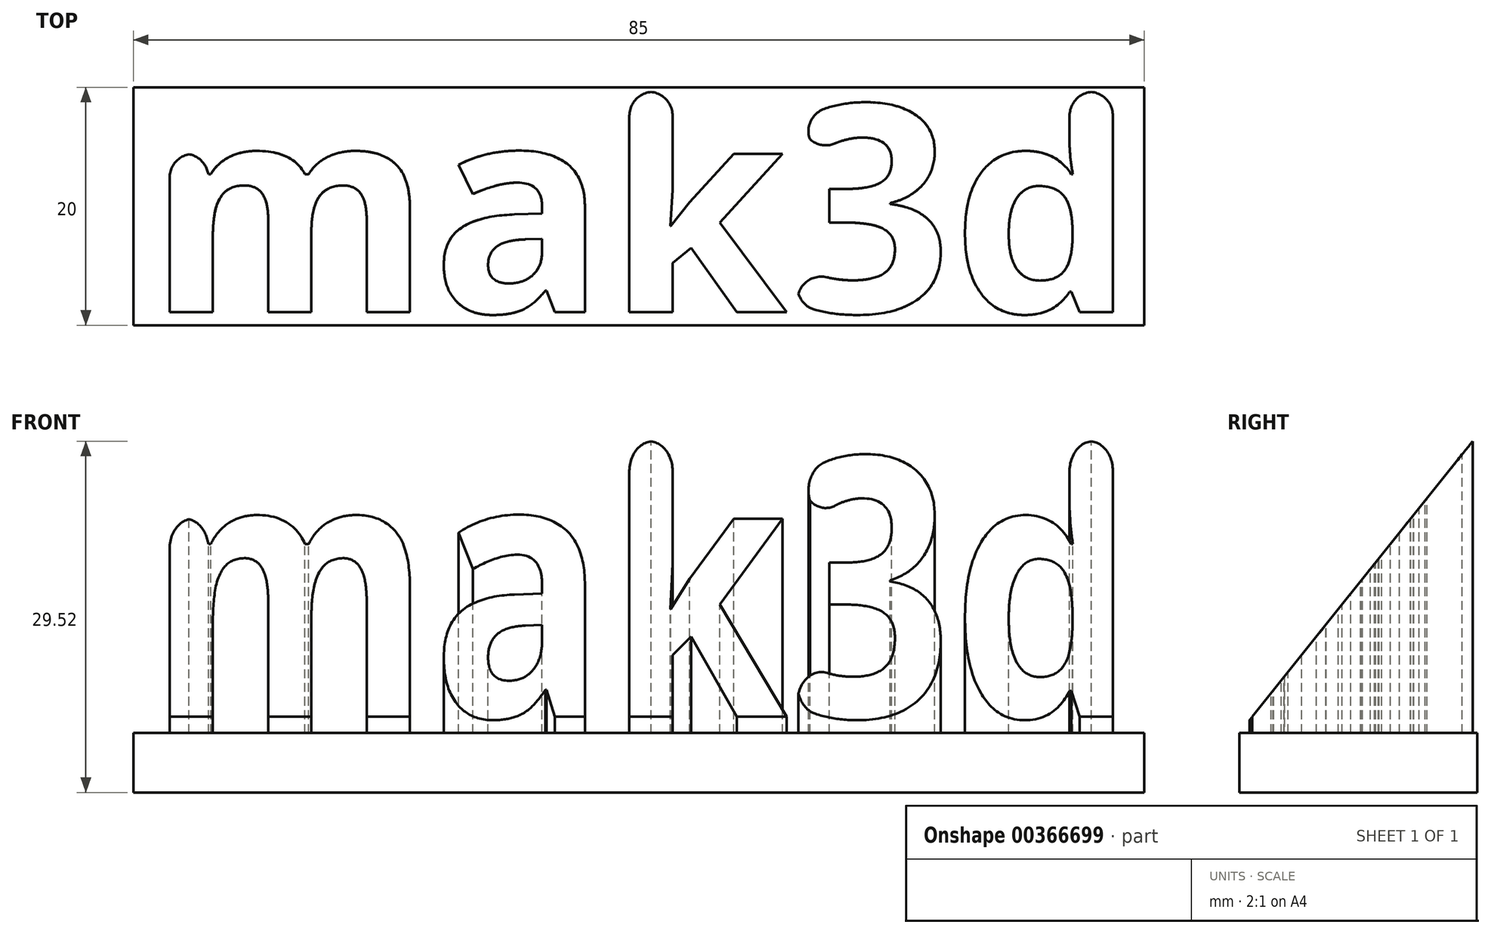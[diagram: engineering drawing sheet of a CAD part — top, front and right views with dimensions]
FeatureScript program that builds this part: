
annotation { "Feature Type Name" : "Feature", "Feature Type Description" : "" }
export const myFeature = defineFeature(function(context is Context, id is Id, definition is map)
    precondition{}
    {
        {
            var Q0;
            Q0=qCreatedBy(makeId("Top.planeOp"),FACE);
            var sketch = newSketch(context, id + "F0", { "sketchPlane" : qUnion([Q0])});
            skLineSegment(sketch, "E0.bottom", {"start": v(0, 0) * mm, "end": v(-100, 0) * mm});
            skLineSegment(sketch, "E0.top", {"start": v(0, 20) * mm, "end": v(-100, 20) * mm});
            skLineSegment(sketch, "E0.left", {"start": v(0, 0) * mm, "end": v(0, 20) * mm});
            skLineSegment(sketch, "E0.right", {"start": v(-100, 0) * mm, "end": v(-100, 20) * mm});
            skSolve(sketch);
        }
        {
            var Q0;
            Q0 = qSketchRegion(id + "F0", true);
            var Q1;
            Q1=makeQuery(id+"F0.imprint","IMPRINT",FACE,{"disambiguationData":[TD([[makeQuery(id+"F0.imprint","IMPRINT",EDGE,{"derivedFrom":sQuery(id+"F0.wireOp",EDGE,"E0.bottom")}),-1.0]])]});
            extrude(context, id + "F1", {"entities" : qUnion([Q0, Q1]), "depth" : 30 * mm});
        }
        {
            var Q0;
            Q0=makeQuery(id+"F1.opExtrude","SWEPT_FACE",FACE,{"disambiguationData":[OSD([sQuery(id+"F0.wireOp",EDGE,"E0.right")])]});
            var sketch = newSketch(context, id + "F2", { "sketchPlane" : qUnion([Q0])});
            skLineSegment(sketch, "E1", {"start": v(0, 0) * mm, "end": v(0, 5) * mm});
            skLineSegment(sketch, "E2", {"start": v(0, 5) * mm, "end": v(-20, 30) * mm});
            skSolve(sketch);
        }
        {
            var Q0;
            Q0=makeQuery(id+"F1.opExtrude","CAP_FACE",FACE,{"disambiguationData":[OSD([sQuery(id+"F0.wireOp",EDGE,"E0.bottom"),sQuery(id+"F0.wireOp",EDGE,"E0.top"),sQuery(id+"F0.wireOp",EDGE,"E0.left"),sQuery(id+"F0.wireOp",EDGE,"E0.right")])],"isStart":false});
            var sketch = newSketch(context, id + "F3", { "sketchPlane" : qUnion([Q0])});
            skText(sketch, "E3", { "text": "mak3d", "fontName": "OpenSans-Bold.ttf"});
            const initialGuessF3  = {"E3": [-0.09885, 0.0011, 1, 0, 0.01755]};
            skSetInitialGuess(sketch, initialGuessF3);
            skSolve(sketch);
        }
        {
            var Q0;
            Q0=makeQuery(id+"F1.opExtrude","SWEPT_FACE",FACE,{"disambiguationData":[OSD([sQuery(id+"F0.wireOp",EDGE,"E0.left")])]});
            extrude(context, id + "F4", {"entities" : qUnion([Q0]), "operationType" : NewBodyOperationType.REMOVE, "oppositeDirection" : true, "depth" : 15 * mm});
        }
        {
            var Q0;
            Q0=makeQuery(id+"F3.imprint","IMPRINT",FACE,{"disambiguationData":[TD([[makeQuery(id+"F3.imprint","IMPRINT",EDGE,{"derivedFrom":sQuery(id+"F3.wireOp",EDGE,"E3.sketch_text.stroke-0")}),1.0]])]});
            var Q1;
            Q1=makeQuery(id+"F3.imprint","IMPRINT",FACE,{"disambiguationData":[TD([[makeQuery(id+"F3.imprint","IMPRINT",EDGE,{"derivedFrom":sQuery(id+"F3.wireOp",EDGE,"E3.sketch_text.stroke-46")}),1.0]])]});
            var Q2;
            Q2=makeQuery(id+"F3.imprint","IMPRINT",FACE,{"disambiguationData":[TD([[makeQuery(id+"F3.imprint","IMPRINT",EDGE,{"derivedFrom":sQuery(id+"F3.wireOp",EDGE,"E3.sketch_text.stroke-109")}),1.0]])]});
            extrude(context, id + "F5", {"entities" : qUnion([Q0, Q1, Q2]), "operationType" : NewBodyOperationType.REMOVE, "oppositeDirection" : true, "depth" : 25 * mm});
        }
        {
            var Q0;
            {var subQ0=sQuery(id+"F2.wireOp",EDGE,"E2");Q0=makeQuery(id+"F2.imprint","IMPRINT",FACE,{"disambiguationData":[TD([[makeQuery(id+"F2.imprint","IMPRINT",EDGE,{"derivedFrom":subQ0}),-1.0]])]});}
            extrude(context, id + "F6", {"entities" : qUnion([Q0]), "operationType" : NewBodyOperationType.REMOVE, "oppositeDirection" : true, "depth" : 200 * mm});
        }
        {
            var Q0;
            Q0=makeQuery(id+"F5.boolean.opBoolean","COPY",EDGE,{"derivedFrom":makeQuery(id+"F5.opExtrude","SWEPT_EDGE",EDGE,{"disambiguationData":[OSD([sQuery(id+"F3.wireOp",EDGE,"E3.sketch_text.stroke-103"),sQuery(id+"F3.wireOp",EDGE,"E3.sketch_text.stroke-104")])]})});
            var Q1;
            Q1=makeQuery(id+"F5.boolean.opBoolean","COPY",EDGE,{"derivedFrom":makeQuery(id+"F5.opExtrude","SWEPT_EDGE",EDGE,{"disambiguationData":[OSD([sQuery(id+"F3.wireOp",EDGE,"E3.sketch_text.stroke-102"),sQuery(id+"F3.wireOp",EDGE,"E3.sketch_text.stroke-103")])]})});
            var Q2;
            Q2=makeQuery(id+"F5.boolean.opBoolean","COPY",EDGE,{"derivedFrom":makeQuery(id+"F5.opExtrude","SWEPT_EDGE",EDGE,{"disambiguationData":[OSD([sQuery(id+"F3.wireOp",EDGE,"E3.sketch_text.stroke-63"),sQuery(id+"F3.wireOp",EDGE,"E3.sketch_text.stroke-64")])]})});
            var Q3;
            Q3=makeQuery(id+"F5.boolean.opBoolean","COPY",EDGE,{"derivedFrom":makeQuery(id+"F5.opExtrude","SWEPT_EDGE",EDGE,{"disambiguationData":[OSD([sQuery(id+"F3.wireOp",EDGE,"E3.sketch_text.stroke-64"),sQuery(id+"F3.wireOp",EDGE,"E3.sketch_text.stroke-65")])]})});
            var Q4;
            Q4=makeQuery(id+"F5.boolean.opBoolean","COPY",EDGE,{"derivedFrom":makeQuery(id+"F5.opExtrude","SWEPT_EDGE",EDGE,{"disambiguationData":[OSD([sQuery(id+"F3.wireOp",EDGE,"E3.sketch_text.stroke-8"),sQuery(id+"F3.wireOp",EDGE,"E3.sketch_text.stroke-9")])]})});
            var Q5;
            Q5=makeQuery(id+"F5.boolean.opBoolean","COPY",EDGE,{"derivedFrom":makeQuery(id+"F5.opExtrude","SWEPT_EDGE",EDGE,{"disambiguationData":[OSD([sQuery(id+"F3.wireOp",EDGE,"E3.sketch_text.stroke-9"),sQuery(id+"F3.wireOp",EDGE,"E3.sketch_text.stroke-10")])]})});
            var Q6;
            Q6=makeQuery(id+"F5.boolean.opBoolean","COPY",EDGE,{"derivedFrom":makeQuery(id+"F5.opExtrude","SWEPT_EDGE",EDGE,{"disambiguationData":[OSD([sQuery(id+"F3.wireOp",EDGE,"E3.sketch_text.stroke-90"),sQuery(id+"F3.wireOp",EDGE,"E3.sketch_text.stroke-91")])]})});
            var Q7;
            Q7=makeQuery(id+"F5.boolean.opBoolean","COPY",EDGE,{"derivedFrom":makeQuery(id+"F5.opExtrude","SWEPT_EDGE",EDGE,{"disambiguationData":[OSD([sQuery(id+"F3.wireOp",EDGE,"E3.sketch_text.stroke-91"),sQuery(id+"F3.wireOp",EDGE,"E3.sketch_text.stroke-92")])]})});
            var Q8;
            Q8=makeQuery(id+"F5.boolean.opBoolean","COPY",EDGE,{"derivedFrom":makeQuery(id+"F5.opExtrude","SWEPT_EDGE",EDGE,{"disambiguationData":[OSD([sQuery(id+"F3.wireOp",EDGE,"E3.sketch_text.stroke-75"),sQuery(id+"F3.wireOp",EDGE,"E3.sketch_text.stroke-76")])]})});
            var Q9;
            Q9=makeQuery(id+"F5.boolean.opBoolean","COPY",EDGE,{"derivedFrom":makeQuery(id+"F5.opExtrude","SWEPT_EDGE",EDGE,{"disambiguationData":[OSD([sQuery(id+"F3.wireOp",EDGE,"E3.sketch_text.stroke-76"),sQuery(id+"F3.wireOp",EDGE,"E3.sketch_text.stroke-77")])]})});
            fillet(context, id + "F7", {"entities" : qUnion([Q0, Q1, Q2, Q3, Q4, Q5, Q6, Q7, Q8, Q9]), "radius" : 2 * mm, "tangentPropagation" : true, "allowEdgeOverflow" : false});
        }
    });
